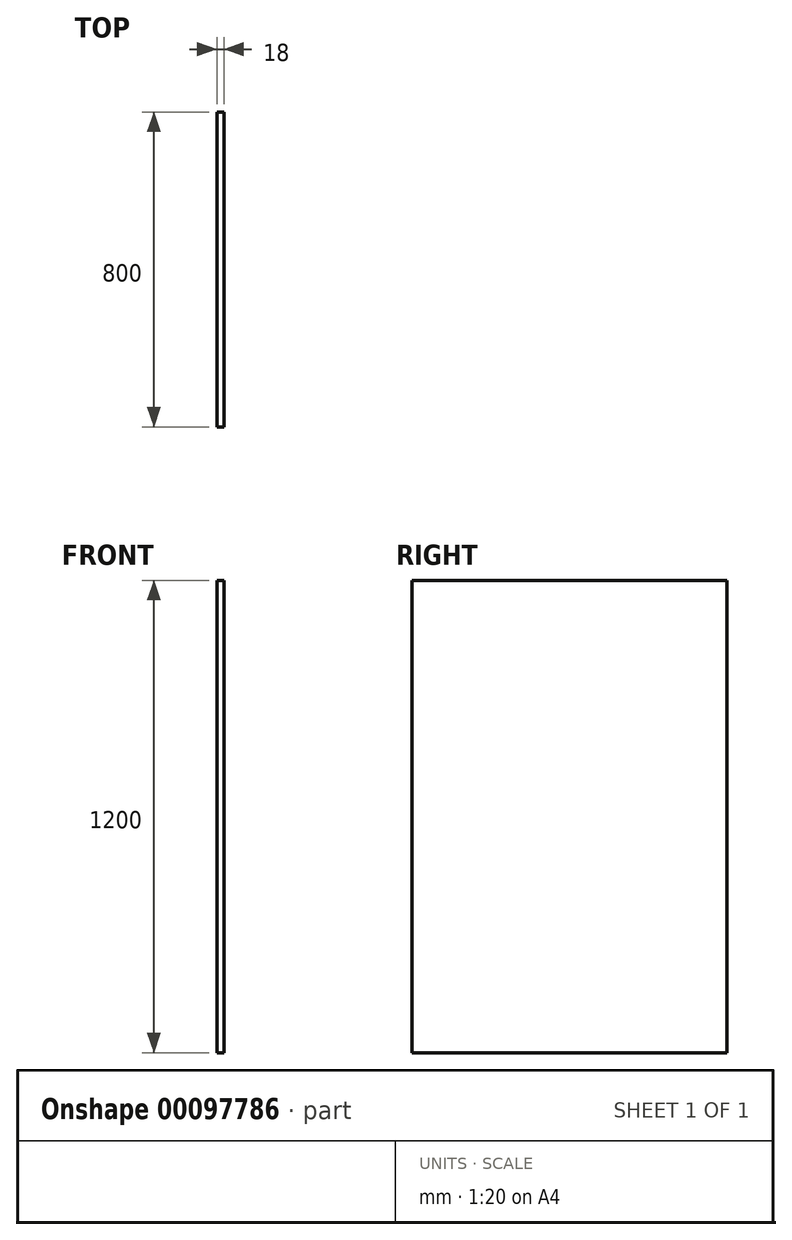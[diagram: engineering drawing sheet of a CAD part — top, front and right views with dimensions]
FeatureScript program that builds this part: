
annotation { "Feature Type Name" : "Feature", "Feature Type Description" : "" }
export const myFeature = defineFeature(function(context is Context, id is Id, definition is map)
    precondition{}
    {
        {
            var Q0;
            Q0=qCreatedBy(makeId("Top.planeOp"),FACE);
            var sketch = newSketch(context, id + "F0", { "sketchPlane" : qUnion([Q0])});
            skLineSegment(sketch, "E0.bottom", {"start": v(0, 0) * mm, "end": v(-18, 0) * mm});
            skLineSegment(sketch, "E0.top", {"start": v(0, 800) * mm, "end": v(-18, 800) * mm});
            skLineSegment(sketch, "E0.left", {"start": v(0, 0) * mm, "end": v(0, 800) * mm});
            skLineSegment(sketch, "E0.right", {"start": v(-18, 0) * mm, "end": v(-18, 800) * mm});
            skSolve(sketch);
        }
        {
            var Q0;
            Q0 = qSketchRegion(id + "F0", true);
            extrude(context, id + "F1", {"entities" : qUnion([Q0]), "depth" : 1200 * mm});
        }
    });
